# Revit family: NBS_DudleyIndustriesLimited_PprTwlDpnsrs_3RollPlasmaRange_77974SS
name_source: partatom
category: Specialty Equipment
units: mm (PartAtom-declared; Revit-internal decimal feet)

## family parameters
Cut with Voids When Loaded = No
Host = Face
Part Type = Normal
Room Calculation Point = No
Round Connector Dimension = Use Diameter
Shared = No

## types (1)
- 77974SS
    AssetType = Fixed
    BIMObjectName = NBS_DudleyIndustriesLimited_ToiletPaperDispensers_3RollPlasmaRange_77974SS
    Category = Pr_40_70_22_90:Toilet paper dispensers
    Color = Brushed / Polished / Powder Coated
    Default Elevation = 1150 mm
    Description = Sleek brushed stainless steel three-roll toilet roll holder
    DispenserDepth = 129 mm  [stored 0.423228 ft]
    DispenserHeight = 405 mm  [stored 1.32874 ft]
    DispenserMaterial = NBS_DudleyIndustries_StainlessSteel_Polished
    DispenserWidth = 126 mm  [stored 0.413386 ft]
    Finish = Brushed / Polished / Powder Coated
    IfcExportAs = IfcFurnitureType
    IfcExportType = NOTDEFINED
    IsBuiltIn = No
    ManufacturerName = Dudley Industries Limited
    ManufacturerURL = www.dudleyindustries.com
    Material = Stainless Steel
    ModelNumber = 77974SS
    ModelReference = Toilet Roll Plasma Dispenser Three Roll 77974SS
    NBSCertification = www.nationalbimlibrary.com/cert/hgd0aidy
    NBSDescription = Paper towel dispensers
    NBSReference = 45-35-72/344
    Name = ToiletPaperDispensers_3RollPlasmaRange_77974SS_DudleyIndustriesLimited_NBS
    NominalDepth = 129 mm  [stored 0.423228 ft]
    NominalHeight = 405 mm  [stored 1.32874 ft]
    NominalLength = 126 mm  [stored 0.413386 ft]
    NominalWidth = 126 mm  [stored 0.413386 ft]
    ProductInformation = https://www.dudleyindustries.com
    Size = 405mm x 126mm x 129mm
    Status = UNSET
    Uniclass2015Code = Pr_40_70_22_62
    Uniclass2015Title = Paper towel dispensers
    Uniclass2015Version = Products v1.22
    Version = 1
    WarrantyDurationUnit = year

note: [stored X ft] marks values corroborated as IEEE doubles in the binary element streams (Revit-internal decimal feet)

## geometry (parser evidence)
native form markers: Sweep x2
no freeform markers — native parametric forms only
